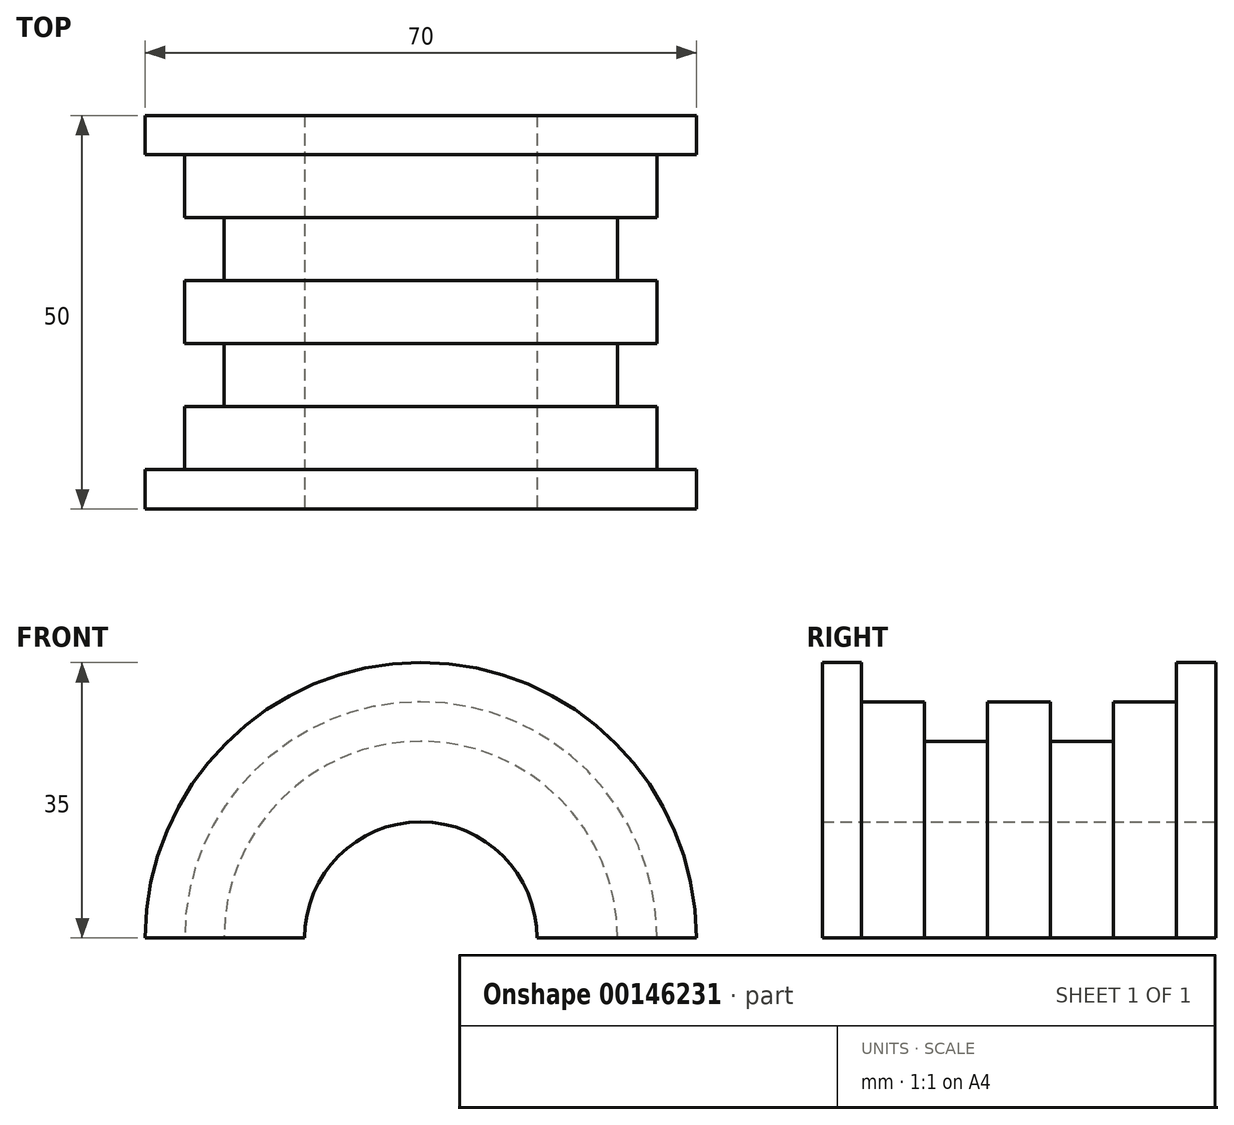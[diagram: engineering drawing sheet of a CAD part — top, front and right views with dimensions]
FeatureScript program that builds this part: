
annotation { "Feature Type Name" : "Feature", "Feature Type Description" : "" }
export const myFeature = defineFeature(function(context is Context, id is Id, definition is map)
    precondition{}
    {
        {
            var Q0;
            Q0=qCreatedBy(makeId("Top.planeOp"),FACE);
            var sketch = newSketch(context, id + "F0", { "sketchPlane" : qUnion([Q0])});
            skLineSegment(sketch, "E0", {"start": v(14.75, 25) * mm, "end": v(14.75, -25) * mm});
            skLineSegment(sketch, "E1", {"start": v(14.75, -25) * mm, "end": v(35, -25) * mm});
            skLineSegment(sketch, "E2", {"start": v(35, -25) * mm, "end": v(35, -20) * mm});
            skLineSegment(sketch, "E3", {"start": v(35, -20) * mm, "end": v(30, -20) * mm});
            skLineSegment(sketch, "E4", {"start": v(30, -20) * mm, "end": v(30, -12) * mm});
            skLineSegment(sketch, "E5", {"start": v(30, -12) * mm, "end": v(25, -12) * mm});
            skLineSegment(sketch, "E6", {"start": v(25, -12) * mm, "end": v(25, -4) * mm});
            skLineSegment(sketch, "E7", {"start": v(25, -4) * mm, "end": v(30, -4) * mm});
            skLineSegment(sketch, "E8", {"start": v(30, -4) * mm, "end": v(30, 4) * mm});
            skLineSegment(sketch, "E9", {"start": v(30, 4) * mm, "end": v(25, 4) * mm});
            skLineSegment(sketch, "E10", {"start": v(25, 4) * mm, "end": v(25, 12) * mm});
            skLineSegment(sketch, "E11", {"start": v(25, 12) * mm, "end": v(30, 12) * mm});
            skLineSegment(sketch, "E12", {"start": v(30, 12) * mm, "end": v(30, 20) * mm});
            skLineSegment(sketch, "E13", {"start": v(30, 20) * mm, "end": v(35, 20) * mm});
            skLineSegment(sketch, "E14", {"start": v(35, 20) * mm, "end": v(35, 25) * mm});
            skLineSegment(sketch, "E15", {"start": v(35, 25) * mm, "end": v(14.75, 25) * mm});
            skLineSegment(sketch, "E16", {"start": v(0, 0) * mm, "end": v(0, -33.48) * mm, "construction": true});
            skSolve(sketch);
        }
        {
            var Q0;
            Q0=makeQuery(id+"F0.imprint","IMPRINT",FACE,{"disambiguationData":[TD([[makeQuery(id+"F0.imprint","IMPRINT",EDGE,{"derivedFrom":sQuery(id+"F0.wireOp",EDGE,"E0")}),1.0]])]});
            var Q1;
            Q1=sQuery(id+"F0.wireOp",EDGE,"E16");
            revolve(context, id + "F1", {"entities" : qUnion([Q0]), "axis" : qUnion([Q1]), "revolveType" : RevolveType.ONE_DIRECTION, "angle" : 180 * degree});
        }
    });
